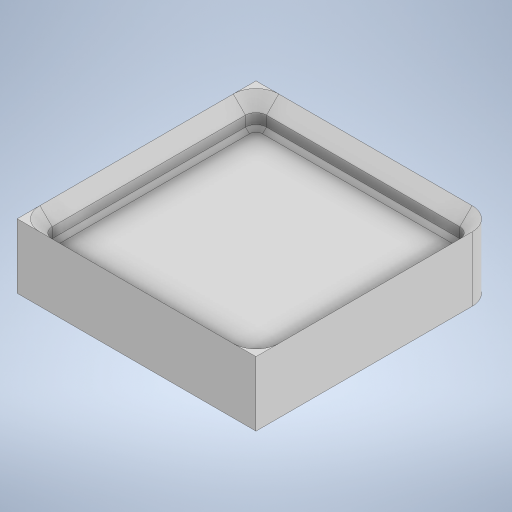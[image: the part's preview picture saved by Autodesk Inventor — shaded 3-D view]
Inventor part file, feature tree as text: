
AUTODESK INVENTOR PART (.ipt)
format: ipt  version: 2023 (Build 270158030, 158C)  size: 330,240 bytes
history: native  units: mm
features: extrude x4, sketch x4, chamfer x2, projected_geometry x1
ambient origin geometry x8: Origin, YZ Plane, XZ Plane, XY Plane, X Axis, Y Axis, Z Axis, Center Point
bodies: Solid1 (feature_tree)
feature tree (11):
  extrude  "square-base"  Depth=42.0mm
  extrude  "Extrusion2"  Depth=4.65mm
  extrude  "Extrusion3"  Depth=2.85mm
  chamfer  "Chamfer2"  [1 undecoded]
  chamfer  "Chamfer1"  Distance=2.15mm
  extrude  "weighted-base"  Depth=2.15mm
  sketch  "Sketch1"  dims[d0=42.0mm d1=42.0mm]
  sketch  "Sketch2"  dims[d2=4.65mm d3=0.0mm d4=2.85mm]
  sketch  "Sketch3"  dims[d5=2.85mm d6=2.85mm]
  sketch  "Sketch5"  dims[d7=2.85mm d8=0.0mm d9=0.0mm d10=2.15mm d12=2.15mm d13=2.15mm d14=2.15mm d15=3.95mm d16=0.0mm d17=2.15mm d18=2.0mm d19=45.0deg d24=0.7mm d25=2.0mm d26=45.0deg d29=1.15mm d30=1.85mm d31=4.0mm d32=6.7mm d33=0.0mm d20=0.872665mm d27=0.0mm]
  projected_geometry  "Projected Loop1"
note: 1 required parameter value undecoded (feature->parameter linkage not recoverable at this tier; creation-order binding heuristic only, values carry confidence <= 0.55)
